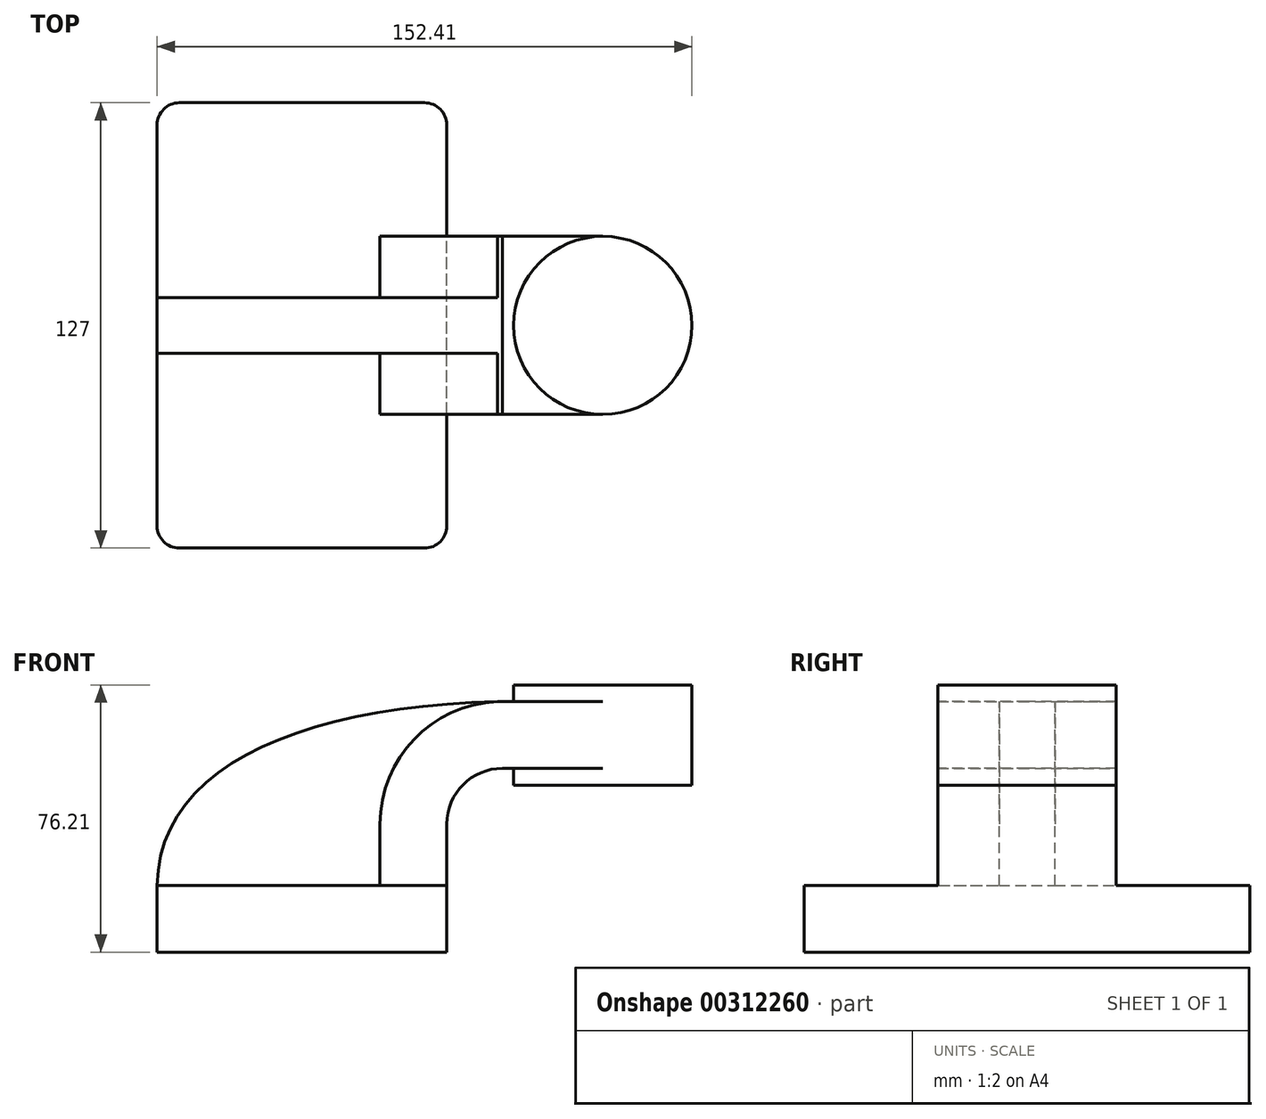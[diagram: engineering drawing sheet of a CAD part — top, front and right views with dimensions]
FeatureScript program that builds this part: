
annotation { "Feature Type Name" : "Feature", "Feature Type Description" : "" }
export const myFeature = defineFeature(function(context is Context, id is Id, definition is map)
    precondition{}
    {
        {
            var Q0;
            Q0=qCreatedBy(makeId("Front.planeOp"),FACE);
            var sketch = newSketch(context, id + "F0", { "sketchPlane" : qUnion([Q0])});
            skLineSegment(sketch, "E0.bottom", {"start": v(41.27, 9.53) * mm, "end": v(-41.28, 9.53) * mm});
            skLineSegment(sketch, "E0.top", {"start": v(41.28, -9.52) * mm, "end": v(-41.27, -9.52) * mm});
            skLineSegment(sketch, "E0.left", {"start": v(41.28, 9.53) * mm, "end": v(41.28, -9.52) * mm});
            skLineSegment(sketch, "E0.right", {"start": v(-41.28, 9.53) * mm, "end": v(-41.27, -9.52) * mm});
            skPoint(sketch, "E0.middle", {"position": v(0, 0) * mm});
            skLineSegment(sketch, "E1.bottom", {"start": v(60.33, 66.68) * mm, "end": v(111.13, 66.68) * mm});
            skLineSegment(sketch, "E1.top", {"start": v(60.33, 38.1) * mm, "end": v(111.13, 38.1) * mm});
            skLineSegment(sketch, "E1.left", {"start": v(60.33, 66.68) * mm, "end": v(60.33, 38.1) * mm});
            skLineSegment(sketch, "E1.right", {"start": v(111.13, 66.68) * mm, "end": v(111.13, 38.1) * mm});
            skPoint(sketch, "E1.middle", {"position": v(85.73, 52.39) * mm});
            skLineSegment(sketch, "E2", {"start": v(41.27, 9.53) * mm, "end": v(41.27, 27) * mm});
            skArc(sketch, "E3", {"start": v(41.27, 27) * mm, "mid": v(45.92, 38.23) * mm, "end": v(57.15, 42.88) * mm});
            skLineSegment(sketch, "E4", {"start": v(57.15, 42.88) * mm, "end": v(85.73, 42.88) * mm});
            skLineSegment(sketch, "E5", {"start": v(85.73, 52.39) * mm, "end": v(85.72, 66.68) * mm});
            skLineSegment(sketch, "E6", {"start": v(85.72, 66.68) * mm, "end": v(85.73, 52.39) * mm});
            skLineSegment(sketch, "E7", {"start": v(85.73, 38.1) * mm, "end": v(85.73, 52.39) * mm});
            skLineSegment(sketch, "E8.0", {"start": v(57.15, 61.93) * mm, "end": v(111.12, 61.93) * mm});
            skArc(sketch, "E8.1", {"start": v(22.23, 27) * mm, "mid": v(32.45, 51.7) * mm, "end": v(57.15, 61.93) * mm});
            skLineSegment(sketch, "E8.2", {"start": v(22.22, 9.53) * mm, "end": v(22.22, 27) * mm});
            skFitSpline(sketch, "E9", {"points": [v(-41.28, 9.53) * mm, v(57.15, 61.93) * mm], "startDerivative": vector(1.68, 102.06) * mm, "endDerivative": vector(171.45, 3.18) * mm});
            skSolve(sketch);
        }
        {
            var Q0;
            Q0=makeQuery(id+"F0.imprint","IMPRINT",FACE,{"disambiguationData":[TD([[makeQuery(id+"F0.imprint","IMPRINT",EDGE,{"derivedFrom":sQuery(id+"F0.wireOp",EDGE,"E0.top")}),-1.0]])]});
            extrude(context, id + "F1", {"entities" : qUnion([Q0]), "endBound" : BoundingType.SYMMETRIC, "depth" : 127 * mm});
        }
        {
            var Q0;
            {var subQ0=sQuery(id+"F0.wireOp",EDGE,"E2");Q0=makeQuery(id+"F0.imprint","IMPRINT",FACE,{"disambiguationData":[TD([[makeQuery(id+"F0.imprint","IMPRINT",EDGE,{"derivedFrom":subQ0}),1.0]])]});}
            extrude(context, id + "F2", {"entities" : qUnion([Q0]), "operationType" : NewBodyOperationType.ADD, "endBound" : BoundingType.SYMMETRIC, "depth" : 50.8 * mm});
        }
        {
            var Q0;
            {var subQ5=sQuery(id+"F0.wireOp",EDGE,"E8.0");var subQ6=sQuery(id+"F0.wireOp",EDGE,"E1.left");var subQ7=makeQuery(id+"F0.imprint","INTERSECT",VERTEX,{"derivedFrom":[subQ6,subQ5]});Q0=makeQuery(id+"F0.imprint","IMPRINT",FACE,{"disambiguationData":[TD([[makeQuery(id+"F0.imprint","IMPRINT",EDGE,{"disambiguationData":[TD([[subQ7,-1.0]])],"derivedFrom":subQ6}),1.0]])]});}
            extrude(context, id + "F3", {"entities" : qUnion([Q0]), "operationType" : NewBodyOperationType.ADD, "endBound" : BoundingType.SYMMETRIC, "depth" : 50.8 * mm});
        }
        {
            var Q0;
            {var subQ3=sQuery(id+"F0.wireOp",EDGE,"E8.2");Q0=makeQuery(id+"F0.imprint","IMPRINT",FACE,{"disambiguationData":[TD([[makeQuery(id+"F0.imprint","IMPRINT",EDGE,{"derivedFrom":subQ3}),1.0]])]});}
            extrude(context, id + "F4", {"entities" : qUnion([Q0]), "operationType" : NewBodyOperationType.ADD, "endBound" : BoundingType.SYMMETRIC, "depth" : 15.88 * mm});
        }
        {
            var Q0;
            {var subQ2=sQuery(id+"F0.wireOp",EDGE,"E1.top");var subQ8=sQuery(id+"F0.wireOp",EDGE,"E1.right");var subQ9=makeQuery(id+"F0.imprint","INTERSECT",VERTEX,{"derivedFrom":[subQ2,subQ8]});Q0=makeQuery(id+"F0.imprint","IMPRINT",FACE,{"disambiguationData":[TD([[makeQuery(id+"F0.imprint","IMPRINT",EDGE,{"disambiguationData":[TD([[subQ9,1.0]])],"derivedFrom":subQ2}),1.0]])]});}
            var Q1;
            {var subQ0=sQuery(id+"F0.wireOp",EDGE,"E1.right");var subQ1=sQuery(id+"F0.wireOp",EDGE,"E1.bottom");var subQ2=makeQuery(id+"F0.imprint","INTERSECT",VERTEX,{"derivedFrom":[subQ1,subQ0]});Q1=makeQuery(id+"F0.imprint","IMPRINT",FACE,{"disambiguationData":[TD([[makeQuery(id+"F0.imprint","IMPRINT",EDGE,{"disambiguationData":[TD([[subQ2,1.0]])],"derivedFrom":subQ1}),-1.0]])]});}
            var Q2;
            Q2=sQuery(id+"F0.wireOp",EDGE,"E7");
            revolve(context, id + "F5", {"operationType" : NewBodyOperationType.ADD, "entities" : qUnion([Q0, Q1]), "axis" : qUnion([Q2]), "revolveType" : RevolveType.FULL});
        }
        {
            var Q0;
            Q0=makeQuery(id+"F1.opExtrude","CAP_EDGE",EDGE,{"disambiguationData":[OSD([sQuery(id+"F0.wireOp",EDGE,"E0.right")])],"isStart":true});
            var Q1;
            Q1=makeQuery(id+"F1.opExtrude","CAP_EDGE",EDGE,{"disambiguationData":[OSD([sQuery(id+"F0.wireOp",EDGE,"E0.right")])],"isStart":false});
            var Q2;
            Q2=makeQuery(id+"F1.opExtrude","CAP_EDGE",EDGE,{"disambiguationData":[OSD([sQuery(id+"F0.wireOp",EDGE,"E0.left")])],"isStart":false});
            var Q3;
            Q3=makeQuery(id+"F1.opExtrude","CAP_EDGE",EDGE,{"disambiguationData":[OSD([sQuery(id+"F0.wireOp",EDGE,"E0.left")])],"isStart":true});
            fillet(context, id + "F6", {"entities" : qUnion([Q0, Q1, Q2, Q3]), "radius" : 6.35 * mm, "tangentPropagation" : true, "allowEdgeOverflow" : false});
        }
    });
